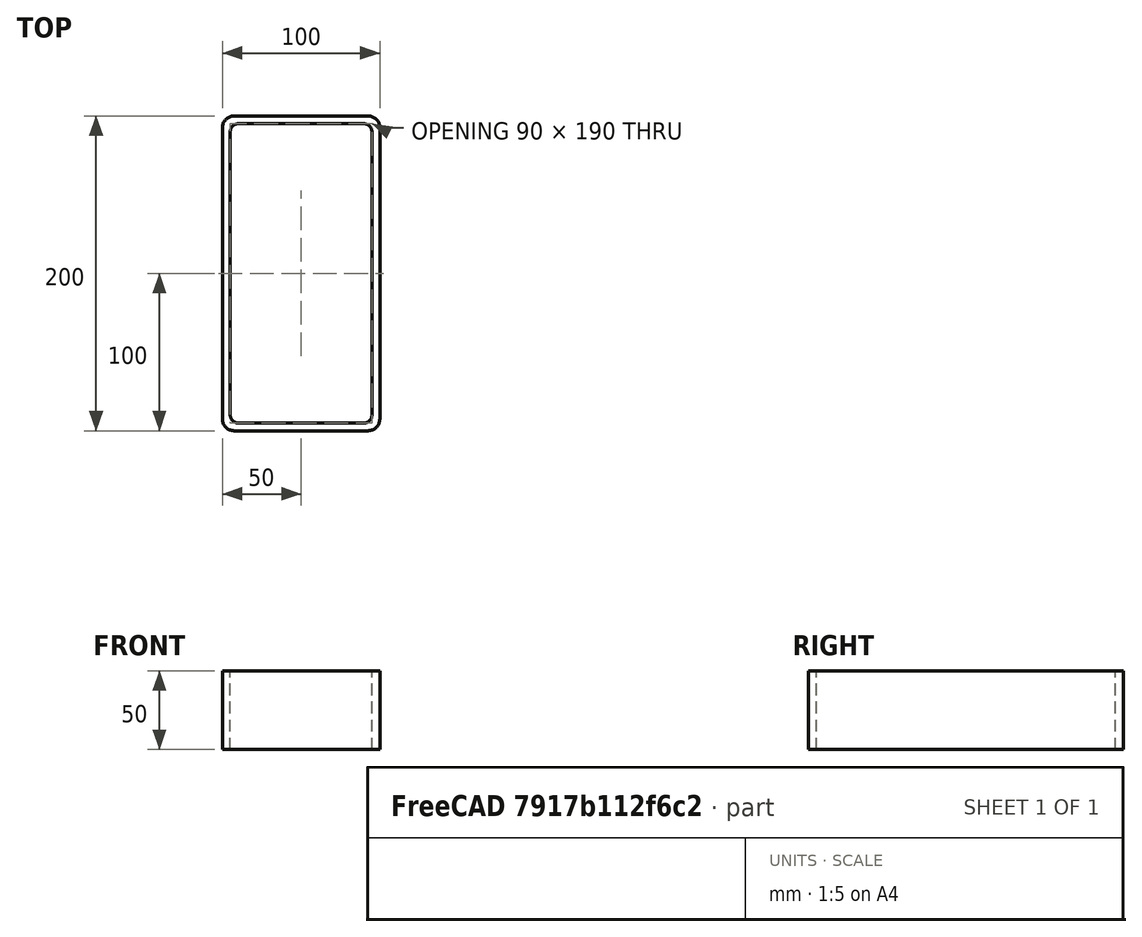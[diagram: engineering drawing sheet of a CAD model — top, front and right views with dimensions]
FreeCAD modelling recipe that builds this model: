
FCSTD DOCUMENT  (FreeCAD 0.15R4671 (Git))
Label: Rectangular hollow section 200x100x5 EN10219 S235JRH
License: All rights reserved
LicenseURL: http://en.wikipedia.org/wiki/All_rights_reserved
objects: Sketcher::SketchObject×1, Part::Extrusion×1
note: 2 computed .brp shape members not serialized (recipe doc carries the construction recipe); baked Part::Feature solids carry a one-line shape summary decoded from their .brp

FEATURE [Sketcher::SketchObject] Sketch
  sketch-geometry (16):
    g0: LineSegment StartX=-40 StartY=95 StartZ=0 EndX=40 EndY=95 EndZ=0
    g1: LineSegment StartX=45 StartY=90 StartZ=0 EndX=45 EndY=-90 EndZ=0
    g2: LineSegment StartX=40 StartY=-95 StartZ=0 EndX=-40 EndY=-95 EndZ=0
    g3: LineSegment StartX=-45 StartY=-90 StartZ=0 EndX=-45 EndY=90 EndZ=0
    g4: LineSegment StartX=-42.5 StartY=100 StartZ=0 EndX=42.5 EndY=100 EndZ=0
    g5: LineSegment StartX=50 StartY=92.5 StartZ=0 EndX=50 EndY=-92.5 EndZ=0
    g6: LineSegment StartX=42.5 StartY=-100 StartZ=0 EndX=-42.5 EndY=-100 EndZ=0
    g7: LineSegment StartX=-50 StartY=-92.5 StartZ=0 EndX=-50 EndY=92.5 EndZ=0
    g8: ArcOfCircle CenterX=-40 CenterY=90 CenterZ=0 NormalX=0 NormalY=0 NormalZ=1 Radius=5 StartAngle=1.5708 EndAngle=3.14159
    g9: ArcOfCircle CenterX=40 CenterY=90 CenterZ=0 NormalX=0 NormalY=0 NormalZ=1 Radius=5 StartAngle=0 EndAngle=1.5708
    g10: ArcOfCircle CenterX=40 CenterY=-90 CenterZ=0 NormalX=0 NormalY=0 NormalZ=1 Radius=5 StartAngle=4.71239 EndAngle=6.28319
    g11: ArcOfCircle CenterX=-40 CenterY=-90 CenterZ=0 NormalX=0 NormalY=0 NormalZ=1 Radius=5 StartAngle=3.14159 EndAngle=4.71239
    g12: ArcOfCircle CenterX=42.5 CenterY=92.5 CenterZ=0 NormalX=0 NormalY=0 NormalZ=1 Radius=7.5 StartAngle=0 EndAngle=1.5708
    g13: ArcOfCircle CenterX=42.5 CenterY=-92.5 CenterZ=0 NormalX=0 NormalY=0 NormalZ=1 Radius=7.5 StartAngle=4.71239 EndAngle=6.28319
    g14: ArcOfCircle CenterX=-42.5 CenterY=-92.5 CenterZ=0 NormalX=0 NormalY=0 NormalZ=1 Radius=7.5 StartAngle=3.14159 EndAngle=4.71239
    g15: ArcOfCircle CenterX=-42.5 CenterY=92.5 CenterZ=0 NormalX=0 NormalY=0 NormalZ=1 Radius=7.5 StartAngle=1.5708 EndAngle=3.14159
  constraints (36):
    c: Horizontal(g2)
    c: Vertical(g3)
    c: Horizontal(g6)
    c: Vertical(g7)
    c: Tangent(g3,g8) = 1.5708
    c: Tangent(g0,g8) = 1.5708
    c: Tangent(g0,g9) = 1.5708
    c: Tangent(g1,g9) = 1.5708
    c: Tangent(g1,g10) = 1.5708
    c: Tangent(g2,g10) = 1.5708
    c: Tangent(g2,g11) = 1.5708
    c: Tangent(g3,g11) = 1.5708
    c: Tangent(g4,g12) = 1.5708
    c: Tangent(g5,g12) = 1.5708
    c: Tangent(g5,g13) = 1.5708
    c: Tangent(g6,g13) = 1.5708
    c: Tangent(g6,g14) = 1.5708
    c: Tangent(g7,g14) = 1.5708
    c: Tangent(g7,g15) = 1.5708
    c: Tangent(g4,g15) = 1.5708
    c: Equal(g9,g8)
    c: Equal(g9,g11)
    c: Equal(g9,g10)
    c: Equal(g12,g15)
    c: Equal(g12,g14)
    c: Equal(g12,g13)
    c: Symmetric(g4,g6,g-1)
    c: Symmetric(g7,g5,g-2)
    c: DistanceY(g4,g6) = -200
    c: DistanceX(g7,g5) = 100
    c: Symmetric(g3,g1,g-2)
    c: Symmetric(g0,g2,g-1)
    c: DistanceY(g0,g4) = 5
    c: DistanceX(g5,g1) = -5
    c: Radius(g9) = 5
    c: Radius(g12) = 7.5
FEATURE [Part::Extrusion] Extrude  label="Rectangular hollow section 200x100x5 EN10219 S235JRH"
  Base = -> Sketch
  Dir = (0,0,50)
  Solid = true
